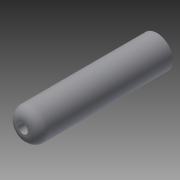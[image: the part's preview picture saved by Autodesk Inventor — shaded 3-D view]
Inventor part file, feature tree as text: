
AUTODESK INVENTOR PART (.ipt)
format: ipt  version: 2013 (Build 170138000, 138)  size: 87,552 bytes
history: native  units: in
note: dims shown in document units (in); Inventor stores cm internally (conversion verified against a paired STEP export)
features: extrude x1, fillet x1, sketch x1
ambient origin geometry x8: Origin, YZ Plane, XZ Plane, XY Plane, X Axis, Y Axis, Z Axis, Center Point
bodies: Solid1 (feature_tree)
feature tree (3):
  extrude  "Extrusion1"  Depth=0.75in
  fillet  "Fillet1"  Radius=10.5in
  sketch  "Sketch1"  dims[d0=2.5in d1=0.75in d2=10.5in d3=0.0in d4=0.75in]
